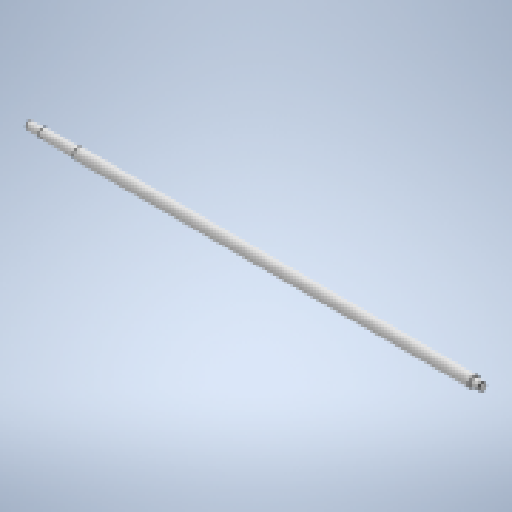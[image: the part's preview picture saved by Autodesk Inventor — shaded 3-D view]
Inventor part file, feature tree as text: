
AUTODESK INVENTOR PART (.ipt)
format: ipt  version: 2023 (Build 270158000, 158)  size: 269,824 bytes
history: native  units: in
note: dims shown in document units (in); Inventor stores cm internally (conversion verified against a paired STEP export)
features: revolve x1, sketch x1
ambient origin geometry x8: Origin, YZ Plane, XZ Plane, XY Plane, X Axis, Y Axis, Z Axis, Center Point
bodies: Solid1 (feature_tree)
feature tree (2):
  revolve  "Revolution1"  [1 undecoded]
  sketch  "Sketch1"  dims[d0=0.1575in d1=0.1969in d2=0.2362in d3=135.0deg d4=135.0deg d5=0.5906in d6=1.5354in d7=135.0deg d8=0.1575in d9=0.2756in d10=0.3937in d11=0.0079in d12=0.0354in d14=135.0deg d15=19.685in d16=90.0deg]
note: 1 required parameter value undecoded (feature->parameter linkage not recoverable at this tier; creation-order binding heuristic only, values carry confidence <= 0.55)
